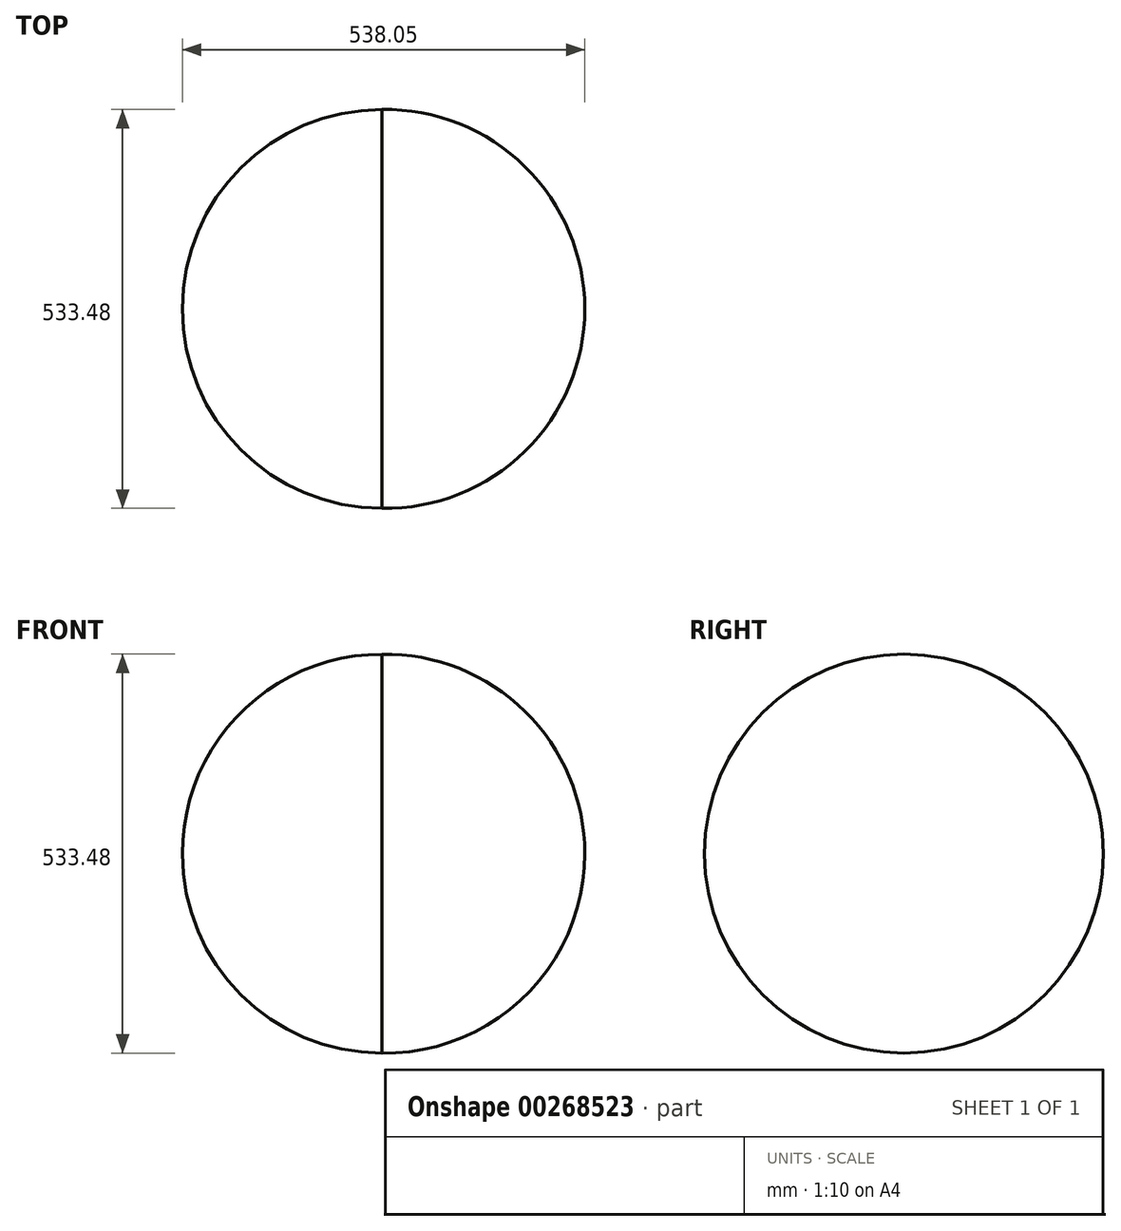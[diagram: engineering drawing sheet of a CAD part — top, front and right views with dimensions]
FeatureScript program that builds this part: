
annotation { "Feature Type Name" : "Feature", "Feature Type Description" : "" }
export const myFeature = defineFeature(function(context is Context, id is Id, definition is map)
    precondition{}
    {
        {
            var Q0;
            Q0=qCreatedBy(makeId("Front.planeOp"),FACE);
            var sketch = newSketch(context, id + "F0", { "sketchPlane" : qUnion([Q0])});
            skLineSegment(sketch, "E0", {"start": v(0, 0) * mm, "end": v(0, 266.7) * mm});
            skArc(sketch, "E1", {"start": v(0, 266.7) * mm, "mid": v(191.59, 190.24) * mm, "end": v(271.35, 0) * mm});
            skArc(sketch, "E2", {"start": v(0, 266.7) * mm, "mid": v(-188.59, 188.59) * mm, "end": v(-266.7, 0) * mm});
            skLineSegment(sketch, "E3", {"start": v(-266.7, 0) * mm, "end": v(271.35, 0) * mm});
            skSolve(sketch);
        }
        {
            var Q0;
            Q0 = qSketchRegion(id + "F0", true);
            var Q1;
            Q1=sQuery(id+"F0.wireOp",EDGE,"E3");
            revolve(context, id + "F1", {"entities" : qUnion([Q0]), "axis" : qUnion([Q1]), "revolveType" : RevolveType.FULL});
        }
    });
